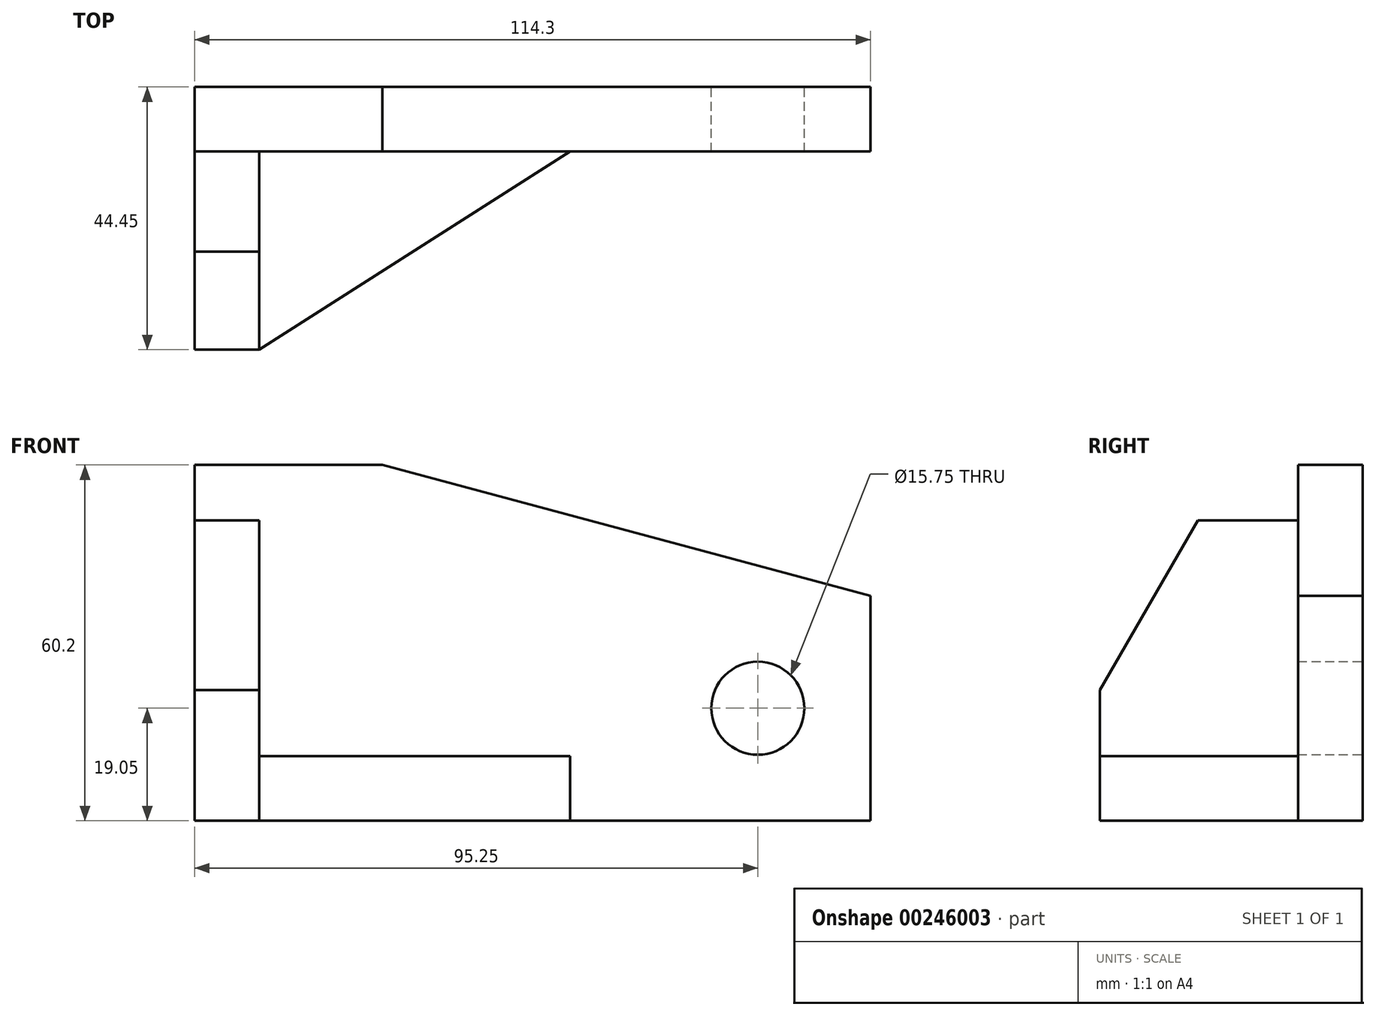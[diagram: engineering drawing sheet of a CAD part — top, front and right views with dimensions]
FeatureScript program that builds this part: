
annotation { "Feature Type Name" : "Feature", "Feature Type Description" : "" }
export const myFeature = defineFeature(function(context is Context, id is Id, definition is map)
    precondition{}
    {
        {
            var Q0;
            Q0=qCreatedBy(makeId("Front.planeOp"),FACE);
            var sketch = newSketch(context, id + "F0", { "sketchPlane" : qUnion([Q0])});
            skLineSegment(sketch, "E0", {"start": v(-57.15, 0) * mm, "end": v(57.15, 0) * mm});
            skLineSegment(sketch, "E1", {"start": v(-57.15, 0) * mm, "end": v(-57.15, 60.2) * mm});
            skLineSegment(sketch, "E2", {"start": v(-57.15, 60.2) * mm, "end": v(-25.4, 60.2) * mm});
            skLineSegment(sketch, "E3", {"start": v(-25.4, 60.2) * mm, "end": v(57.15, 38.08) * mm});
            skLineSegment(sketch, "E4", {"start": v(57.15, 38.08) * mm, "end": v(57.15, 0) * mm});
            skLineSegment(sketch, "E5", {"start": v(-25.4, 60.2) * mm, "end": v(57.15, 60.2) * mm, "construction": true});
            skLineSegment(sketch, "E6", {"start": v(57.15, 0) * mm, "end": v(38.1, 0) * mm, "construction": true});
            skLineSegment(sketch, "E7", {"start": v(38.1, 0) * mm, "end": v(38.1, 19.05) * mm, "construction": true});
            skCircle(sketch, "E8", {"center": v(38.1, 19.05) * mm, "radius": 7.87 * mm});
            skSolve(sketch);
        }
        {
            var Q0;
            Q0 = qSketchRegion(id + "F0", true);
            extrude(context, id + "F1", {"entities" : qUnion([Q0]), "depth" : 10.92 * mm});
        }
        {
            var Q0;
            Q0=makeQuery(id+"F1.opExtrude","SWEPT_FACE",FACE,{"disambiguationData":[OSD([sQuery(id+"F0.wireOp",EDGE,"E1")])]});
            var sketch = newSketch(context, id + "F2", { "sketchPlane" : qUnion([Q0])});
            skLineSegment(sketch, "E9", {"start": v(10.92, 0) * mm, "end": v(10.92, 50.8) * mm, "construction": true});
            skLineSegment(sketch, "E10", {"start": v(0, 0) * mm, "end": v(44.45, 0) * mm});
            skLineSegment(sketch, "E11", {"start": v(44.45, 0) * mm, "end": v(44.45, 22.1) * mm});
            skLineSegment(sketch, "E12", {"start": v(44.45, 0) * mm, "end": v(44.45, 50.8) * mm, "construction": true});
            skLineSegment(sketch, "E13", {"start": v(44.45, 22.1) * mm, "end": v(27.88, 50.8) * mm});
            skLineSegment(sketch, "E14", {"start": v(27.88, 50.8) * mm, "end": v(10.92, 50.8) * mm});
            skSolve(sketch);
        }
        {
            var Q0;
            Q0 = qSketchRegion(id + "F2", true);
            var Q1;
            {var subQ1=sQuery(id+"F2.wireOp",EDGE,"E11");Q1=makeQuery(id+"F2.imprint","IMPRINT",FACE,{"disambiguationData":[TD([[makeQuery(id+"F2.imprint","IMPRINT",EDGE,{"derivedFrom":subQ1}),1.0]])]});}
            extrude(context, id + "F3", {"entities" : qUnion([Q0, Q1]), "operationType" : NewBodyOperationType.ADD, "oppositeDirection" : true, "depth" : 10.92 * mm});
        }
        {
            var Q0;
            Q0=makeQuery(id+"F3.boolean.opBoolean","MERGE",FACE,{"derivedFrom":[makeQuery(id+"F1.opExtrude","SWEPT_FACE",FACE,{"disambiguationData":[OSD([sQuery(id+"F0.wireOp",EDGE,"E0")])]}),makeQuery(id+"F3.opExtrude","SWEPT_FACE",FACE,{"disambiguationData":[OSD([sQuery(id+"F2.wireOp",EDGE,"E10")])]})]});
            var sketch = newSketch(context, id + "F4", { "sketchPlane" : qUnion([Q0])});
            skLineSegment(sketch, "E15", {"start": v(-57.15, 0) * mm, "end": v(6.35, 0) * mm, "construction": true});
            skLineSegment(sketch, "E16", {"start": v(6.35, 10.92) * mm, "end": v(-46.23, 44.45) * mm});
            skSolve(sketch);
        }
        {
            var Q0;
            {var subQ0=sQuery(id+"F4.wireOp",EDGE,"E16");Q0=makeQuery(id+"F4.imprint","IMPRINT",FACE,{"disambiguationData":[TD([[makeQuery(id+"F4.imprint","IMPRINT",EDGE,{"derivedFrom":subQ0}),1.0]])]});}
            extrude(context, id + "F5", {"entities" : qUnion([Q0]), "operationType" : NewBodyOperationType.ADD, "oppositeDirection" : true, "depth" : 10.92 * mm});
        }
    });
